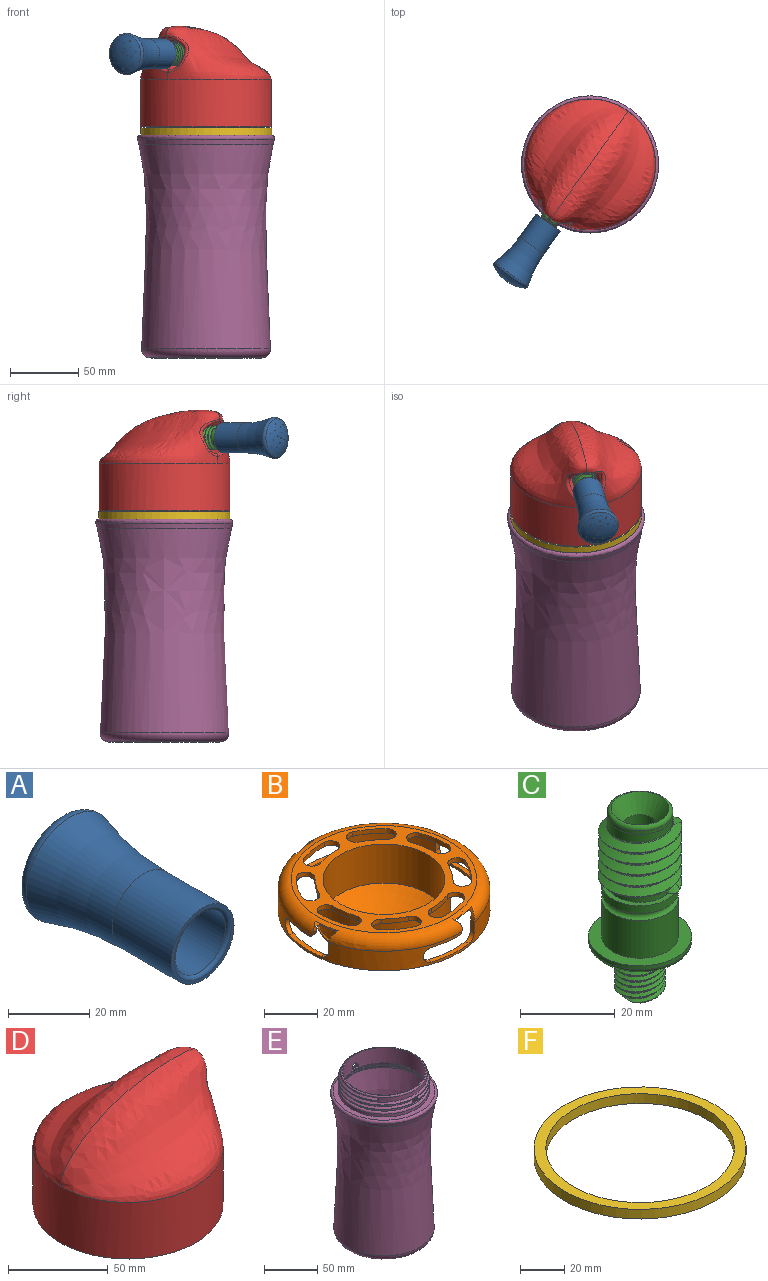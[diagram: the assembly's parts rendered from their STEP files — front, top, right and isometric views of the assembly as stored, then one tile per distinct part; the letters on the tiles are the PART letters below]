
ASSEMBLY  parts=6 mates=5
PART A: 110 faces, bbox 86.1x101.6x86.1 mm
  f0: extruded ~1.03x0.49mm, area 0.8mm2, adj f2,f16,f79
  f1: extruded ~1.04x0.47mm, area 0.8mm2, adj f2,f16,f77
  f2: torus R=1.43mm, axis (0,-1,0), area 391.8mm2, adj f0,f1,f13,f14,f15,f35,f36,f37
  f3: cylinder r=8.89mm len=17.79mm, axis (0,1,0), area 754.3mm2, adj f4,f17,f89,f106,f107
  f4: cylinder r=8.89mm len=17.79mm, axis (0,1,0), area 61.1mm2, adj f3,f5,f28,f89,f107
  f5: cylinder r=8.89mm len=2.15mm, axis (0,1,0), area 0.2mm2, adj f4,f28,f89
  f6: torus R=9.33mm, axis (0,-1,0), area 66.9mm2, adj f10,f11,f21,f80,f81,f82,f86,f96
  f7: cylinder r=6.94mm len=13.89mm, axis (0,-1,0), area 54.7mm2, adj f89,f105,f106,f107
  f8: torus R=93.6mm, axis (0,-1,0), area 2017.2mm2, adj f18,f51
  f9: torus R=6.29mm, axis (0,-1,0), area 48.2mm2, adj f26,f29,f30,f31,f32,f83,f87,f88
  f10: plane 18.2x18.2mm, normal (0,1,0), area 99.4mm2, adj f6,f11,f22,f80,f82,f83,f86,f87
  f11: plane 3.28x2.1mm, normal (0.37,0,0.93), area 7.1mm2, adj f6,f10,f30,f81,f87,f91
  f12: cylinder r=0.24mm len=1.03mm, axis (0.17,0.99,-0.03), area 0.2mm2, adj f13,f15,f16,f56
  f13: extruded ~1.08x0.28mm, area 0.2mm2, adj f2,f12,f15,f16,f93
  f14: extruded ~1.22x0.6mm, area 0.8mm2, adj f2,f15,f16,f40
  f15: torus R=10.15mm, axis (0,-1,0), area 155.7mm2, adj f2,f12,f13,f14,f40,f42,f44,f47
  f16: torus R=1.43mm, axis (0,-1,0), area 652.8mm2, adj f0,f1,f12,f13,f14,f35,f36,f37
  f17: torus R=9.89mm, axis (0,-1,0), area 91.4mm2, adj f3,f52
  f18: cylinder r=10.89mm len=21.79mm, axis (0,1,0), area 1401.3mm2, adj f8,f52
  f19: cylinder r=13mm len=26mm, axis (0,1,0), area 81.7mm2, adj f20,f92
  f20: cone r=12mm half-angle=90deg, axis (0,1,0), area 78.5mm2, adj f19,f21
  f21: torus R=126.22mm, axis (0,-1,0), area 608.6mm2, adj f6,f20
  f22: torus R=4.43mm, axis (0,-1,0), area 35.8mm2, adj f10,f23
  f23: cone r=2.93mm half-angle=4.1deg, axis (0,1,0), area 138.8mm2, adj f22,f24
  f24: torus R=1.93mm, axis (0,-1,0), area 24mm2, adj f23,f34
  f25: torus R=3.88mm, axis (0,-1,0), area 44.6mm2, adj f26,f33
  f26: cone r=5.4mm half-angle=4.1deg, axis (0,1,0), area 227.9mm2, adj f9,f25
  f27: torus R=8.77mm, axis (0,-1,0), area 100.3mm2, adj f28,f29,f30,f31,f32,f90,f91,f97
  f28: torus R=123.58mm, axis (0,-1,0), area 813.1mm2, adj f4,f5,f27,f53
  f29: plane 3.73x3.47mm, normal (0,-1,0), area 7.5mm2, adj f9,f27,f86,f96
  f30: plane 3.73x3.47mm, normal (0,-1,0), area 7.5mm2, adj f9,f11,f27,f82
  f31: plane 3.73x3.47mm, normal (0,-1,0), area 7.5mm2, adj f9,f27,f98,f99
  f32: plane 3.73x3.47mm, normal (0,-1,0), area 7.5mm2, adj f9,f27,f80,f100
  f33: plane 7.58x7.58mm, normal (0,-1,0), area 45.2mm2, adj f25
  f34: plane 3.86x3.86mm, normal (0,1,0), area 11.7mm2, adj f24
  f35: cylinder r=0.25mm len=1mm, axis (0,1,0), area 1.6mm2, adj f2,f16
  f36: extruded ~1.15x0.61mm, area 0.8mm2, adj f2,f16,f75
  f37: extruded ~1.09x0.55mm, area 0.8mm2, adj f2,f16,f74
  f38: extruded ~1.12x0.57mm, area 0.9mm2, adj f2,f16,f73
  f39: extruded ~1.1x0.5mm, area 0.8mm2, adj f2,f16,f72
  f40: extruded ~1.22x0.6mm, area 0.8mm2, adj f2,f14,f15,f16
  f41: extruded ~1.15x0.57mm, area 0.8mm2, adj f2,f16,f71
  f42: extruded ~1.24x0.71mm, area 0.8mm2, adj f2,f15,f16,f70
  f43: extruded ~1.13x0.6mm, area 0.8mm2, adj f2,f16,f69
  f44: extruded ~1.21x0.68mm, area 0.8mm2, adj f2,f15,f16,f68
  f45: extruded ~1.14x0.52mm, area 0.8mm2, adj f2,f16,f67
  f46: extruded ~1.09x0.56mm, area 0.8mm2, adj f2,f16,f66
  f47: extruded ~1.15x0.51mm, area 0.8mm2, adj f2,f15,f16,f65
  f48: torus R=5.32mm, axis (0,-1,0), area 176.4mm2, adj f15,f85
  f49: torus R=12.65mm, axis (0,-1,0), area 31.6mm2, adj f50,f85
  f50: cylinder r=12.9mm len=25.8mm, axis (0,1,0), area 60.8mm2, adj f49,f92
  f51: torus R=12.73mm, axis (0,-1,0), area 268.3mm2, adj f8,f16
  f52: plane 21.79x21.79mm, normal (0,-1,0), area 65.3mm2, adj f17,f18
  f53: cylinder r=8.89mm len=17.79mm, axis (0,-1,0), area 120.8mm2, adj f28,f89,f105,f107
  f54: extruded ~1.06x0.48mm, area 0.8mm2, adj f2,f16,f76
  f55: cylinder r=0.28mm len=1.1mm, axis (0.17,0.99,-0.03), area 0.2mm2, adj f2,f16,f56,f95
  f56: bspline ~1.09x0.34mm, area 0.2mm2, adj f2,f12,f15,f16,f55
  f57: extruded ~1.08x0.33mm, area 0.2mm2, adj f2,f15,f16,f58,f64
  f58: cylinder r=0.28mm len=1.1mm, axis (0.12,0.99,0.11), area 0.2mm2, adj f2,f16,f57,f59
  f59: bspline ~1.08x0.31mm, area 0.2mm2, adj f2,f16,f58,f60
  f60: cylinder r=0.24mm len=1.02mm, axis (0.12,0.99,0.11), area 0.2mm2, adj f2,f16,f59,f61
  f61: extruded ~1.07x0.33mm, area 0.2mm2, adj f2,f16,f60,f62
  f62: cylinder r=0.28mm len=1.1mm, axis (0.12,0.99,0.11), area 0.2mm2, adj f2,f16,f61,f63
  f63: bspline ~1.09x0.31mm, area 0.2mm2, adj f2,f15,f16,f62,f64
  f64: cylinder r=0.24mm len=1.03mm, axis (0.12,0.99,0.11), area 0.2mm2, adj f15,f16,f57,f63
  f65: extruded ~1.14x0.51mm, area 0.8mm2, adj f2,f16,f47
  f66: extruded ~1.09x0.55mm, area 0.8mm2, adj f2,f16,f46
  f67: extruded ~1.14x0.52mm, area 0.8mm2, adj f2,f16,f45
  f68: extruded ~1.2x0.68mm, area 0.8mm2, adj f2,f15,f16,f44
  f69: extruded ~1.13x0.6mm, area 0.8mm2, adj f2,f16,f43
  f70: extruded ~1.24x0.71mm, area 0.8mm2, adj f2,f15,f16,f42
  f71: extruded ~1.15x0.57mm, area 0.8mm2, adj f2,f16,f41
  f72: extruded ~1.1x0.5mm, area 0.8mm2, adj f2,f16,f39
  f73: extruded ~1.12x0.57mm, area 0.8mm2, adj f2,f15,f16,f38
  f74: extruded ~1.1x0.55mm, area 0.8mm2, adj f2,f16,f37
  f75: extruded ~1.15x0.61mm, area 0.8mm2, adj f2,f16,f36
  f76: extruded ~1.06x0.48mm, area 0.8mm2, adj f2,f16,f54
  f77: extruded ~1.04x0.47mm, area 0.8mm2, adj f1,f2,f16
  f78: extruded ~1.06x0.48mm, area 0.8mm2, adj f2,f16,f104
  f79: extruded ~1.03x0.49mm, area 0.8mm2, adj f0,f2,f16
  f80: plane 3.28x2.1mm, normal (-0.93,0,0.37), area 7.1mm2, adj f6,f10,f32,f88,f90,f102
  f81: cylinder r=9.76mm len=10.6mm, axis (0,1,0), area 25.8mm2, adj f6,f11,f86,f91
  f82: plane 3.28x2.1mm, normal (-0.37,0,-0.93), area 7.1mm2, adj f6,f10,f30,f88,f90,f102
  f83: cylinder r=6.29mm len=6mm, axis (0,1,0), area 13.7mm2, adj f9,f10,f98,f100
  f84: cylinder r=0.24mm len=1.02mm, axis (0.17,0.99,-0.03), area 0.2mm2, adj f2,f16,f94,f95
  f85: plane 25.3x25.3mm, normal (0,-1,0), area 54.8mm2, adj f48,f49
  f86: plane 3.28x2.1mm, normal (-0.93,0,0.37), area 7.1mm2, adj f6,f10,f29,f81,f87,f91
  f87: cylinder r=6.29mm len=6mm, axis (0,1,0), area 13.7mm2, adj f9,f10,f11,f86
  f88: cylinder r=6.29mm len=6mm, axis (0,1,0), area 13.7mm2, adj f9,f10,f80,f82
  f89: bspline ~17.78x17.54mm, area 338mm2, adj f3,f4,f5,f7,f53,f105,f106
  f90: plane 10.6x5.13mm, normal (0,1,0), area 11.4mm2, adj f27,f80,f82,f102
  f91: plane 10.6x5.13mm, normal (0,1,0), area 11.4mm2, adj f11,f27,f81,f86
  f92: plane 26x26mm, normal (0,-1,0), area 8.1mm2, adj f19,f50
  f93: cylinder r=0.28mm len=1.1mm, axis (0.17,0.99,-0.03), area 0.2mm2, adj f2,f13,f16,f94
  f94: bspline ~1.09x0.34mm, area 0.2mm2, adj f2,f16,f84,f93
  f95: bspline ~1.07x0.27mm, area 0.2mm2, adj f2,f16,f55,f84
  f96: plane 3.28x2.1mm, normal (0.93,0,-0.37), area 7.1mm2, adj f6,f10,f29,f101,f108,f109
  f97: plane 10.6x5.13mm, normal (0,1,0), area 11.4mm2, adj f27,f98,f100,f103
  f98: plane 3.28x2.1mm, normal (-0.37,0,-0.93), area 7.1mm2, adj f6,f10,f31,f83,f97,f103
  f99: plane 3.28x2.1mm, normal (0.37,0,0.93), area 7.1mm2, adj f6,f10,f31,f101,f108,f109
  f100: plane 3.28x2.1mm, normal (0.93,0,-0.37), area 7.1mm2, adj f6,f10,f32,f83,f97,f103
  f101: cylinder r=9.76mm len=10.6mm, axis (0,1,0), area 25.8mm2, adj f6,f96,f99,f108
  f102: cylinder r=9.76mm len=10.6mm, axis (0,1,0), area 25.8mm2, adj f6,f80,f82,f90
  f103: cylinder r=9.76mm len=10.6mm, axis (0,1,0), area 25.8mm2, adj f6,f97,f98,f100
  f104: extruded ~1.06x0.48mm, area 0.8mm2, adj f2,f16,f78
  f105: plane 1.81x1.5mm, normal (-0.37,0,-0.93), area 1.8mm2, adj f7,f53,f89,f107
  f106: bspline ~4.52x3.66mm, area 5.5mm2, adj f3,f7,f89,f107
  f107: bspline ~17.78x17.77mm, area 384.7mm2, adj f3,f4,f7,f53,f105,f106
  f108: plane 10.6x5.13mm, normal (0,1,0), area 11.4mm2, adj f27,f96,f99,f101
  f109: cylinder r=6.29mm len=6mm, axis (0,1,0), area 13.7mm2, adj f9,f10,f96,f99
PART B: 85 faces, bbox 86.6x86.6x26.4 mm
  f0: plane 76x76mm, normal (0,0,-1), area 1526.1mm2, adj f1,f2,f8,f11,f12,f13,f14,f15
  f1: cylinder r=38mm len=76mm, axis (0,0,-1), area 2065.4mm2, adj f0,f2,f7,f45,f46,f47,f48,f49
  f2: cylinder r=38mm len=4.17mm, axis (0,0,-1), area 7mm2, adj f0,f1,f59,f61,f64
  f3: cylinder r=40mm len=80mm, axis (0,0,-1), area 1563.6mm2, adj f4,f5,f7,f45,f46,f47,f48,f49
  f4: cylinder r=40mm len=1.64mm, axis (0,0,-1), area 1.4mm2, adj f3,f5,f59,f61
  f5: torus R=35mm, axis (0,0,-1), area 1689.2mm2, adj f3,f4,f6,f50,f51,f53,f54,f60
  f6: plane 70x70mm, normal (0,0,1), area 1206.9mm2, adj f5,f10,f11,f12,f13,f14,f15,f16
  f7: plane 80x80mm, normal (0,0,-1), area 490.1mm2, adj f1,f3
  f8: cylinder r=25mm len=50mm, axis (0,0,-1), area 2509mm2, adj f0,f43
  f9: torus R=0.83mm, axis (0,0,-1), area 1797.8mm2, adj f10
  f10: cylinder r=23mm len=46mm, axis (0,0,-1), area 2601.2mm2, adj f6,f9
  f11: cylinder r=35.71mm len=10.27mm, axis (0,0,-1), area 20.9mm2, adj f0,f6,f12,f14
  f12: cylinder r=3.5mm len=7mm, axis (0,0,-1), area 22mm2, adj f0,f6,f11,f13
  f13: cylinder r=34.42mm len=13.03mm, axis (0,0,-1), area 26.6mm2, adj f0,f6,f12,f14
  f14: cylinder r=3.5mm len=6.77mm, axis (0,0,-1), area 22mm2, adj f0,f6,f11,f13
  f15: cylinder r=35.71mm len=10.27mm, axis (0,0,-1), area 20.9mm2, adj f0,f6,f16,f18
  f16: cylinder r=3.5mm len=7mm, axis (0,0,-1), area 22mm2, adj f0,f6,f15,f17
  f17: cylinder r=34.42mm len=13.03mm, axis (0,0,-1), area 26.6mm2, adj f0,f6,f16,f18
  f18: cylinder r=3.5mm len=6.77mm, axis (0,0,-1), area 22mm2, adj f0,f6,f15,f17
  f19: cylinder r=35.71mm len=8.46mm, axis (0,0,-1), area 20.9mm2, adj f0,f6,f20,f22
  f20: cylinder r=3.5mm len=6.06mm, axis (0,0,-1), area 22mm2, adj f0,f6,f19,f21
  f21: cylinder r=34.42mm len=10.74mm, axis (0,0,-1), area 26.6mm2, adj f0,f6,f20,f22
  f22: cylinder r=3.5mm len=6.7mm, axis (0,0,-1), area 22mm2, adj f0,f6,f19,f21
  f23: cylinder r=35.71mm len=10.27mm, axis (0,0,-1), area 20.9mm2, adj f0,f6,f24,f26
  f24: cylinder r=3.5mm len=7mm, axis (0,0,-1), area 22mm2, adj f0,f6,f23,f25
  f25: cylinder r=34.42mm len=13.03mm, axis (0,0,-1), area 26.6mm2, adj f0,f6,f24,f26
  f26: cylinder r=3.5mm len=6.77mm, axis (0,0,-1), area 22mm2, adj f0,f6,f23,f25
  f27: cylinder r=35.71mm len=8.46mm, axis (0,0,-1), area 20.9mm2, adj f0,f6,f28,f30
  f28: cylinder r=3.5mm len=6.06mm, axis (0,0,-1), area 22mm2, adj f0,f6,f27,f29
  f29: cylinder r=34.42mm len=10.74mm, axis (0,0,-1), area 26.6mm2, adj f0,f6,f28,f30
  f30: cylinder r=3.5mm len=6.7mm, axis (0,0,-1), area 22mm2, adj f0,f6,f27,f29
  f31: cylinder r=35.71mm len=8.46mm, axis (0,0,-1), area 20.9mm2, adj f0,f6,f32,f34
  f32: cylinder r=3.5mm len=6.06mm, axis (0,0,-1), area 22mm2, adj f0,f6,f31,f33
  f33: cylinder r=34.42mm len=10.74mm, axis (0,0,-1), area 26.6mm2, adj f0,f6,f32,f34
  f34: cylinder r=3.5mm len=6.7mm, axis (0,0,-1), area 22mm2, adj f0,f6,f31,f33
  f35: cylinder r=35.71mm len=10.27mm, axis (0,0,-1), area 20.9mm2, adj f0,f6,f36,f38
  f36: cylinder r=3.5mm len=7mm, axis (0,0,-1), area 22mm2, adj f0,f6,f35,f37
  f37: cylinder r=34.42mm len=13.03mm, axis (0,0,-1), area 26.6mm2, adj f0,f6,f36,f38
  f38: cylinder r=3.5mm len=6.77mm, axis (0,0,-1), area 22mm2, adj f0,f6,f35,f37
  f39: cylinder r=35.71mm len=8.46mm, axis (0,0,-1), area 20.9mm2, adj f0,f6,f40,f42
  f40: cylinder r=3.5mm len=6.06mm, axis (0,0,-1), area 22mm2, adj f0,f6,f39,f41
  f41: cylinder r=34.42mm len=10.74mm, axis (0,0,-1), area 26.6mm2, adj f0,f6,f40,f42
  f42: cylinder r=3.5mm len=6.7mm, axis (0,0,-1), area 22mm2, adj f0,f6,f39,f41
  f43: torus R=25mm, axis (0,0,-1), area 278.3mm2, adj f8,f44
  f44: torus R=0.83mm, axis (0,0,-1), area 2140.1mm2, adj f43
  f45: cylinder r=3.37mm len=6.75mm, axis (0,-1,0), area 22.9mm2, adj f1,f3,f46,f49
  f46: plane 18.25x4.08mm, normal (0,0,1), area 37mm2, adj f1,f3,f45,f47
  f47: cylinder r=3.35mm len=3.38mm, axis (0,-1,0), area 10.9mm2, adj f1,f3,f46,f48
  f48: plane 3.38x2.06mm, normal (-1,0,0), area 6.9mm2, adj f1,f3,f47,f50
  f49: plane 12.85x4.08mm, normal (0,0,-1), area 26.1mm2, adj f1,f3,f45,f51
  f50: cylinder r=9.38mm len=5.68mm, axis (0,-1,0), area 11.7mm2, adj f0,f1,f3,f5,f48,f52,f53
  f51: cylinder r=2.94mm len=2.49mm, axis (0,-1,0), area 6mm2, adj f1,f3,f5,f49,f54
  f52: cylinder r=40mm len=10.66mm, axis (0,0,-1), area 14.5mm2, adj f0,f50,f53,f54
  f53: plane 10.66x2.74mm, normal (0,0,-1), area 11.9mm2, adj f5,f50,f52,f54
  f54: cylinder r=3.83mm len=3.81mm, axis (0,-1,0), area 6.7mm2, adj f0,f1,f5,f51,f52,f53
  f55: cylinder r=3.37mm len=6.75mm, axis (-1,0,0), area 22.9mm2, adj f1,f3,f56,f59
  f56: plane 18.25x4.08mm, normal (0,0,1), area 37mm2, adj f1,f3,f55,f57
  f57: cylinder r=3.35mm len=3.38mm, axis (-1,0,0), area 10.9mm2, adj f1,f3,f56,f58
  f58: plane 3.38x2.06mm, normal (0,1,0), area 6.9mm2, adj f1,f3,f57,f60
  f59: plane 12.85x4.08mm, normal (0,0,-1), area 26.1mm2, adj f1,f2,f3,f4,f55,f61
  f60: cylinder r=9.38mm len=5.68mm, axis (-1,0,0), area 11.7mm2, adj f0,f1,f3,f5,f58,f62,f63
  f61: cylinder r=2.94mm len=2.49mm, axis (-1,0,0), area 6mm2, adj f2,f4,f5,f59,f64
  f62: cylinder r=40mm len=10.66mm, axis (0,0,-1), area 14.5mm2, adj f0,f60,f63,f64
  f63: plane 10.66x2.74mm, normal (0,0,-1), area 11.9mm2, adj f5,f60,f62,f64
  f64: cylinder r=3.83mm len=3.81mm, axis (-1,0,0), area 6.7mm2, adj f0,f2,f5,f61,f62,f63
  f65: plane 18.25x4.08mm, normal (0,0,1), area 37mm2, adj f1,f3,f66,f68
  f66: cylinder r=3.35mm len=3.38mm, axis (0,1,0), area 10.9mm2, adj f1,f3,f65,f67
  f67: plane 3.38x2.06mm, normal (1,0,0), area 6.9mm2, adj f1,f3,f66,f70
  f68: cylinder r=3.37mm len=6.75mm, axis (0,1,0), area 22.9mm2, adj f1,f3,f65,f69
  f69: plane 12.85x4.08mm, normal (0,0,-1), area 26.1mm2, adj f1,f3,f68,f71
  f70: cylinder r=9.38mm len=5.68mm, axis (0,1,0), area 11.7mm2, adj f0,f1,f3,f5,f67,f72,f73
  f71: cylinder r=2.94mm len=2.49mm, axis (0,1,0), area 6mm2, adj f1,f3,f5,f69,f74
  f72: cylinder r=40mm len=10.66mm, axis (0,0,-1), area 14.5mm2, adj f0,f70,f73,f74
  f73: plane 10.66x2.74mm, normal (0,0,-1), area 11.9mm2, adj f5,f70,f72,f74
  f74: cylinder r=3.83mm len=3.81mm, axis (0,1,0), area 6.7mm2, adj f0,f1,f5,f71,f72,f73
  f75: plane 18.25x4.08mm, normal (0,0,1), area 37mm2, adj f1,f3,f76,f78
  f76: cylinder r=3.35mm len=3.38mm, axis (1,0,0), area 10.9mm2, adj f1,f3,f75,f77
  f77: plane 3.38x2.06mm, normal (0,-1,0), area 6.9mm2, adj f1,f3,f76,f80
  f78: cylinder r=3.37mm len=6.75mm, axis (1,0,0), area 22.9mm2, adj f1,f3,f75,f79
  f79: plane 12.85x4.08mm, normal (0,0,-1), area 26.1mm2, adj f1,f3,f78,f81
  f80: cylinder r=9.38mm len=5.68mm, axis (1,0,0), area 11.7mm2, adj f0,f1,f3,f5,f77,f82,f83
  f81: cylinder r=2.94mm len=2.49mm, axis (1,0,0), area 6mm2, adj f1,f3,f5,f79,f84
  f82: cylinder r=40mm len=10.66mm, axis (0,0,-1), area 14.5mm2, adj f0,f80,f83,f84
  f83: plane 10.66x2.74mm, normal (0,0,-1), area 11.9mm2, adj f5,f80,f82,f84
  f84: cylinder r=3.83mm len=3.81mm, axis (1,0,0), area 6.7mm2, adj f0,f1,f5,f81,f82,f83
PART C: 42 faces, bbox 23.7x23.7x47.7 mm
  f0: cylinder r=5.35mm len=11.54mm, axis (0,0,-1), area 16.3mm2, adj f3,f17,f32,f39
  f1: cylinder r=5.35mm len=11.54mm, axis (0,0,-1), area 16.3mm2, adj f3,f17,f35,f40
  f2: cylinder r=5.35mm len=11.54mm, axis (0,0,-1), area 16.3mm2, adj f3,f17,f31,f36
  f3: plane 10.22x10.07mm, normal (0,0,-1), area 40.7mm2, adj f0,f1,f2,f28,f30,f31,f32,f34
  f4: cylinder r=6.86mm len=13.72mm, axis (0,0,1), area 172.2mm2, adj f8,f9,f10,f12,f27
  f5: cylinder r=6.86mm len=13.72mm, axis (0,0,1), area 89.4mm2, adj f6,f9,f11,f12,f24
  f6: cylinder r=6.86mm len=13.72mm, axis (0,0,1), area 60.9mm2, adj f5,f7,f9,f12
  f7: cylinder r=6.86mm len=13.72mm, axis (0,0,1), area 60.9mm2, adj f6,f8,f9,f12
  f8: cylinder r=6.86mm len=13.72mm, axis (0,0,1), area 60.9mm2, adj f4,f7,f9,f12
  f9: bspline ~14.47x13.96mm, area 56.8mm2, adj f4,f5,f6,f7,f8,f10,f11,f21
  f10: bspline ~3.93x2.92mm, area 1.5mm2, adj f4,f9,f12,f22
  f11: bspline ~3.26x1.86mm, area 1.2mm2, adj f5,f9,f12,f26
  f12: bspline ~17.61x17.57mm, area 494.8mm2, adj f4,f5,f6,f7,f8,f10,f11,f22
  f13: torus R=8mm, axis (0,0,-1), area 142.2mm2, adj f14,f15
  f14: cylinder r=8.1mm len=16.2mm, axis (0,0,1), area 101.8mm2, adj f13,f24
  f15: cylinder r=8.1mm len=16.2mm, axis (0,0,1), area 496.3mm2, adj f13,f25
  f16: cylinder r=10.89mm len=21.78mm, axis (0,0,1), area 68.1mm2, adj f25,f29
  f17: cone r=10.89mm half-angle=89.8deg, axis (0,0,-1), area 217.1mm2, adj f0,f1,f2,f29,f33,f37,f41
  f18: cone r=5.12mm half-angle=34.8deg, axis (0,0,1), area 144.5mm2, adj f19,f28
  f19: torus R=5.95mm, axis (0,0,-1), area 57.8mm2, adj f18,f20
  f20: cone r=6.95mm half-angle=0.8deg, axis (0,0,-1), area 38.5mm2, adj f19,f27
  f21: bspline ~18.52x17.62mm, area 526.6mm2, adj f9,f22,f23,f26
  f22: bspline ~3.87x3.56mm, area 6.3mm2, adj f10,f12,f21,f23
  f23: cylinder r=8.81mm len=17.62mm, axis (0,0,1), area 41mm2, adj f12,f21,f22,f26
  f24: plane 16.2x16.2mm, normal (0,0,1), area 58.4mm2, adj f5,f14
  f25: plane 21.78x21.78mm, normal (0,0,1), area 166.4mm2, adj f15,f16
  f26: bspline ~3.88x3.21mm, area 4.6mm2, adj f11,f12,f21,f23
  f27: plane 13.92x13.92mm, normal (0,0,-1), area 4.3mm2, adj f4,f20
  f28: cylinder r=3.35mm len=42.59mm, axis (0,0,-1), area 896.4mm2, adj f3,f18
  f29: torus R=9.89mm, axis (0,0,1), area 104.1mm2, adj f16,f17
  f30: bspline ~13.05x10.59mm, area 30.8mm2, adj f3,f31,f32,f33
  f31: bspline ~13.14x12.36mm, area 75.6mm2, adj f2,f3,f30,f33
  f32: bspline ~13.14x12.36mm, area 75.6mm2, adj f0,f3,f30,f33
  f33: plane 8.69x2.34mm, normal (0,0,-1), area 4.7mm2, adj f17,f30,f31,f32
  f34: bspline ~13.05x10.59mm, area 30.8mm2, adj f3,f35,f36,f37
  f35: bspline ~13.14x12.36mm, area 75.6mm2, adj f1,f3,f34,f37
  f36: bspline ~13.14x12.36mm, area 75.6mm2, adj f2,f3,f34,f37
  f37: plane 7.48x4.92mm, normal (0,0,-1), area 4.7mm2, adj f17,f34,f35,f36
  f38: bspline ~13.05x10.59mm, area 30.8mm2, adj f3,f39,f40,f41
  f39: bspline ~13.14x12.36mm, area 75.6mm2, adj f0,f3,f38,f41
  f40: bspline ~13.14x12.36mm, area 75.6mm2, adj f1,f3,f38,f41
  f41: plane 7.61x4.76mm, normal (0,0,-1), area 4.7mm2, adj f17,f38,f39,f40
PART D: 62 faces, bbox 102.2x103.7x78.6 mm
  f0: plane 23.06x23.06mm, normal (1,0,0), area 340.5mm2, adj f47,f50,f51,f52,f53,f54,f55,f56
  f1: plane 28.04x28.04mm, normal (-1,0,0), area 540.1mm2, adj f38,f50,f51,f52,f53,f54,f55,f56
  f2: cylinder r=3.2mm len=6.4mm, axis (-1,0,0), area 46.9mm2, adj f4,f28,f29
  f3: plane 3.9x3.9mm, normal (-1,0,0), area 11.9mm2, adj f4
  f4: torus R=1.95mm, axis (-1,0,0), area 33.9mm2, adj f2,f3
  f5: cylinder r=3.2mm len=6.4mm, axis (0,1,0), area 46.9mm2, adj f7,f28,f32
  f6: plane 3.9x3.9mm, normal (0,1,0), area 11.9mm2, adj f7
  f7: torus R=1.95mm, axis (0,1,0), area 33.9mm2, adj f5,f6
  f8: cylinder r=42.75mm len=85.5mm, axis (0,0,1), area 686.4mm2, adj f9,f13,f21,f23
  f9: cylinder r=42.75mm len=85.5mm, axis (0,0,1), area 753.6mm2, adj f8,f10,f23,f25
  f10: cylinder r=42.75mm len=85.5mm, axis (0,0,1), area 753.6mm2, adj f9,f11,f23,f25
  f11: cylinder r=42.75mm len=85.5mm, axis (0,0,1), area 1273.7mm2, adj f10,f22,f25,f27
  f12: cylinder r=47.75mm len=95.5mm, axis (0,0,1), area 10418.4mm2, adj f13,f45,f46
  f13: plane 95.5x95.5mm, normal (0,0,-1), area 1421.6mm2, adj f8,f12
  f14: cylinder r=3.2mm len=6.4mm, axis (0,-1,0), area 47.3mm2, adj f16,f28,f33
  f15: plane 3.9x3.9mm, normal (0,-1,0), area 11.9mm2, adj f16
  f16: torus R=1.95mm, axis (0,-1,0), area 33.9mm2, adj f14,f15
  f17: cylinder r=3.2mm len=6.4mm, axis (1,0,0), area 47.6mm2, adj f19,f28,f36
  f18: plane 3.9x3.9mm, normal (1,0,0), area 11.9mm2, adj f19
  f19: torus R=1.95mm, axis (1,0,0), area 33.9mm2, adj f17,f18
  f20: cylinder r=42.75mm len=85.5mm, axis (0,0,1), area 1608.6mm2, adj f26,f37
  f21: plane 2.2x1.92mm, normal (0,-1,0), area 2.2mm2, adj f8,f23,f24,f25
  f22: plane 2.2x1.92mm, normal (0,1,0), area 2.2mm2, adj f11,f23,f24,f25
  f23: bspline ~98.73x85.5mm, area 2132.1mm2, adj f8,f9,f10,f21,f22,f24
  f24: bspline ~94.54x81.87mm, area 176.8mm2, adj f21,f22,f23,f25
  f25: bspline ~98.73x85.5mm, area 1432.2mm2, adj f9,f10,f11,f21,f22,f24
  f26: plane 85.5x85.5mm, normal (0,0,1), area 542.1mm2, adj f20,f28
  f27: plane 85.5x85.5mm, normal (0,0,-1), area 27.9mm2, adj f11,f29,f30,f31,f32,f33,f34,f35
  f28: cylinder r=40.68mm len=81.36mm, axis (0,0,-1), area 1111.3mm2, adj f2,f5,f14,f17,f26,f30,f31,f34
  f29: bspline ~6.8x2.2mm, area 11mm2, adj f2,f27,f30,f31
  f30: torus R=42.68mm, axis (0,0,1), area 186.3mm2, adj f27,f28,f29,f32
  f31: torus R=42.68mm, axis (0,0,1), area 186.3mm2, adj f27,f28,f29,f33
  f32: bspline ~6.8x2.2mm, area 11mm2, adj f5,f27,f30,f34
  f33: bspline ~6.8x2.2mm, area 11mm2, adj f14,f27,f31,f35
  f34: torus R=42.68mm, axis (0,0,1), area 186.3mm2, adj f27,f28,f32,f36
  f35: torus R=42.68mm, axis (0,0,1), area 186.3mm2, adj f27,f28,f33,f36
  f36: bspline ~6.8x2.2mm, area 11mm2, adj f17,f27,f34,f35
  f37: cone r=42.75mm half-angle=45deg, axis (0,0,1), area 977.4mm2, adj f20,f39,f40,f41,f42,f43,f44
  f38: cylinder r=13.96mm len=35.37mm, axis (1,0,0), area 3032.5mm2, adj f1,f41,f43
  f39: plane 45.26x45.26mm, normal (0,0,-1), area 5.6mm2, adj f37,f43
  f40: plane 22.06x7.28mm, normal (0,0,-1), area 0.1mm2, adj f37,f41
  f41: offset ~102.17x52.73mm, area 4783.7mm2, adj f37,f38,f40,f42,f43
  f42: plane 45.26x45.26mm, normal (0,0,-1), area 5.6mm2, adj f37,f41
  f43: offset ~102.22x52.75mm, area 4783.1mm2, adj f37,f38,f39,f41,f44
  f44: plane 22.06x7.28mm, normal (0,0,-1), area 0.1mm2, adj f37,f43
  f45: bspline ~97.22x47.75mm, area 5457.7mm2, adj f12,f46,f49
  f46: bspline ~97.22x47.75mm, area 5457.7mm2, adj f12,f45,f48
  f47: cylinder r=11.46mm len=30.32mm, axis (1,0,0), area 1967.9mm2, adj f0,f48,f49
  f48: bspline ~26.74x16mm, area 164.6mm2, adj f46,f47,f49
  f49: bspline ~26.74x16mm, area 164.7mm2, adj f45,f47,f48
  f50: bspline ~11.84x10.26mm, area 34.8mm2, adj f0,f1,f52,f59
  f51: bspline ~11.84x10.26mm, area 34.8mm2, adj f0,f1,f52,f60
  f52: bspline ~11.96x10.36mm, area 8.6mm2, adj f0,f1,f50,f51
  f53: bspline ~11.84x10.26mm, area 34.8mm2, adj f0,f1,f55,f60
  f54: bspline ~11.84x10.26mm, area 34.8mm2, adj f0,f1,f55,f61
  f55: bspline ~11.96x10.36mm, area 8.6mm2, adj f0,f1,f53,f54
  f56: bspline ~11.84x10.26mm, area 34.8mm2, adj f0,f1,f58,f61
  f57: bspline ~11.84x10.26mm, area 34.8mm2, adj f0,f1,f58,f59
  f58: bspline ~11.96x10.36mm, area 8.6mm2, adj f0,f1,f56,f57
  f59: cylinder r=4.51mm len=9.02mm, axis (-1,0,0), area 13mm2, adj f0,f1,f50,f57
  f60: cylinder r=4.51mm len=9.02mm, axis (-1,0,0), area 13mm2, adj f0,f1,f51,f53
  f61: cylinder r=4.51mm len=9.02mm, axis (-1,0,0), area 13mm2, adj f0,f1,f54,f56
PART E: 52 faces, bbox 156.4x156.4x200.2 mm
  f0: cylinder r=40.55mm len=81.09mm, axis (0,0,-1), area 770.2mm2, adj f24,f25,f26,f27,f28,f29,f30,f31
  f1: cylinder r=40.55mm len=81.09mm, axis (0,0,-1), area 736.8mm2, adj f2,f4,f5,f36,f37,f47
  f2: cylinder r=40.55mm len=81.09mm, axis (0,0,-1), area 739.6mm2, adj f1,f3,f28,f46,f47,f51
  f3: cylinder r=40.55mm len=64.16mm, axis (0,0,-1), area 249mm2, adj f2,f27,f46,f51
  f4: cone r=0mm half-angle=44.1deg, axis (0,0,-1), area 2.7mm2, adj f1,f5,f47
  f5: revolved ~2.68x0.84mm, area 0.7mm2, adj f1,f4,f37,f49
  f6: cylinder r=38.55mm len=77.09mm, axis (0,0,-1), area 4148.6mm2, adj f7,f24,f25,f26,f27,f28,f29,f30
  f7: plane 78.09x78.09mm, normal (0,0,1), area 121.9mm2, adj f6,f36
  f8: torus R=134.41mm, axis (0,0,-1), area 1277.1mm2, adj f9,f13
  f9: revolved ~149.61x94.06mm, area 40584.3mm2, adj f8,f10
  f10: torus R=40.58mm, axis (0,0,-1), area 1565.2mm2, adj f9,f11
  f11: torus R=40.33mm, axis (0,0,-1), area 529.3mm2, adj f10,f12
  f12: torus R=1.47mm, axis (0,0,-1), area 5048.2mm2, adj f11
  f13: revolved ~96.18x96.18mm, area 184.7mm2, adj f8,f14
  f14: plane 95.61x95.61mm, normal (0,0,-1), area 1492.6mm2, adj f13,f34
  f15: cylinder r=40.55mm len=81.09mm, axis (0,0,-1), area 339.8mm2, adj f32,f34
  f16: torus R=134.41mm, axis (0,0,-1), area 1299.5mm2, adj f17,f21
  f17: revolved ~149.07x97.96mm, area 42311.1mm2, adj f16,f18
  f18: torus R=40.58mm, axis (0,0,-1), area 2352.7mm2, adj f17,f19
  f19: torus R=40.33mm, axis (0,0,-1), area 750.6mm2, adj f18,f20
  f20: torus R=1.47mm, axis (0,0,-1), area 5008.5mm2, adj f19
  f21: revolved ~100.18x100.18mm, area 1341.8mm2, adj f16,f22
  f22: plane 95.54x95.54mm, normal (0,0,1), area 1483mm2, adj f21,f23
  f23: cylinder r=42.55mm len=85.09mm, axis (0,0,-1), area 891.2mm2, adj f22,f33
  f24: plane 3.93x3.01mm, normal (-1,0,0), area 8.1mm2, adj f0,f6,f25,f27,f40,f41,f42
  f25: plane 8x2.21mm, normal (0,0,1), area 16mm2, adj f0,f6,f24,f26
  f26: plane 3.93x3.01mm, normal (1,0,0), area 8.1mm2, adj f0,f6,f25,f27,f44,f45,f46
  f27: cylinder r=4mm len=8mm, axis (0,1,0), area 33.1mm2, adj f0,f3,f6,f24,f26,f42,f46,f47
  f28: cylinder r=4mm len=8mm, axis (0,1,0), area 30mm2, adj f0,f2,f6,f29,f31,f44,f45,f46
  f29: plane 3x2.01mm, normal (1,0,0), area 6mm2, adj f0,f6,f28,f30
  f30: plane 8x2.21mm, normal (0,0,1), area 16mm2, adj f0,f6,f29,f31
  f31: plane 3x2.01mm, normal (-1,0,0), area 6mm2, adj f0,f6,f28,f30
  f32: torus R=38.55mm, axis (0,0,-1), area 529mm2, adj f15,f35
  f33: torus R=40.55mm, axis (0,0,-1), area 825.5mm2, adj f0,f23,f43
  f34: torus R=42.55mm, axis (0,0,-1), area 814.7mm2, adj f14,f15
  f35: torus R=40.55mm, axis (0,0,1), area 511.8mm2, adj f6,f32
  f36: torus R=39.05mm, axis (0,0,1), area 592.2mm2, adj f1,f7
  f37: plane 2.67x1.97mm, normal (0,0,-1), area 2.9mm2, adj f1,f5,f49,f51
  f38: torus R=1.79mm, axis (0,0,-1), area 0.9mm2, adj f0,f39,f40,f41,f43
  f39: cone r=0mm half-angle=44.1deg, axis (0,0,-1), area 6.6mm2, adj f0,f38,f42
  f40: bspline ~63.51x48.89mm, area 107.6mm2, adj f0,f24,f38,f41
  f41: bspline ~63.72x49.05mm, area 14.6mm2, adj f24,f38,f40,f42
  f42: bspline ~63.62x48.97mm, area 164.1mm2, adj f0,f24,f27,f39,f41
  f43: plane 3.59x1.83mm, normal (0,0,-1), area 5.1mm2, adj f33,f38
  f44: bspline ~97.78x63.51mm, area 219.3mm2, adj f0,f26,f28,f45
  f45: bspline ~98.11x63.72mm, area 29.3mm2, adj f26,f28,f44,f46
  f46: bspline ~97.94x63.62mm, area 329.7mm2, adj f2,f3,f26,f27,f28,f45
  f47: bspline ~97.94x84.82mm, area 1281.7mm2, adj f1,f2,f4,f27,f28,f48,f49
  f48: bspline ~98.11x63.72mm, area 29.7mm2, adj f27,f28,f47,f50
  f49: bspline ~84.86x84.84mm, area 83.6mm2, adj f5,f27,f37,f47,f51
  f50: bspline ~97.78x63.51mm, area 222.1mm2, adj f0,f27,f28,f48
  f51: bspline ~97.78x84.68mm, area 626.1mm2, adj f2,f3,f27,f37,f49
PART F: 4 faces, bbox 95.8x95.8x5.3 mm
  f0: cylinder r=42.55mm len=85.09mm, axis (0,0,1), area 1425.9mm2, adj f2,f3
  f1: cylinder r=47.88mm len=95.76mm, axis (0,0,1), area 1604.6mm2, adj f2,f3
  f2: plane 95.76x95.76mm, normal (0,0,1), area 1515.3mm2, adj f0,f1
  f3: plane 95.76x95.76mm, normal (0,0,-1), area 1515.3mm2, adj f0,f1
PLACE A rot(axis=(-0.95,0.31,0),180deg) t=(-26.85,-37.42,65.83)mm
PLACE B t=(0,0,-41.55)mm
PLACE C rot(axis=(0.42,-0.81,0.42),102deg) t=(-11.97,-16.68,65.83)mm
PLACE D rot(axis=(0,0,-1),125.7deg) t=(0,0,2.83)mm
PLACE E at identity fixed
PLACE F t=(0,0,9.25)mm
MATE fastened C.f17 <-> D.f38  axis (0.58,0.81,0) through (-9.91,-13.81,65.83)mm
MATE fastened F.f0 <-> E.f10  axis (0,0,-1) through (0,0,6.58)mm
MATE slider C.f18 <-> A.f3  axis (-0.58,-0.81,0) through (-29.18,-40.66,65.83)mm
MATE cylindrical F.f0 <-> D.f8  axis (0,0,1) through (0,0,11.91)mm
MATE cylindrical B.f1 <-> D.f8  axis (0,0,-1) through (0,0,-22)mm
